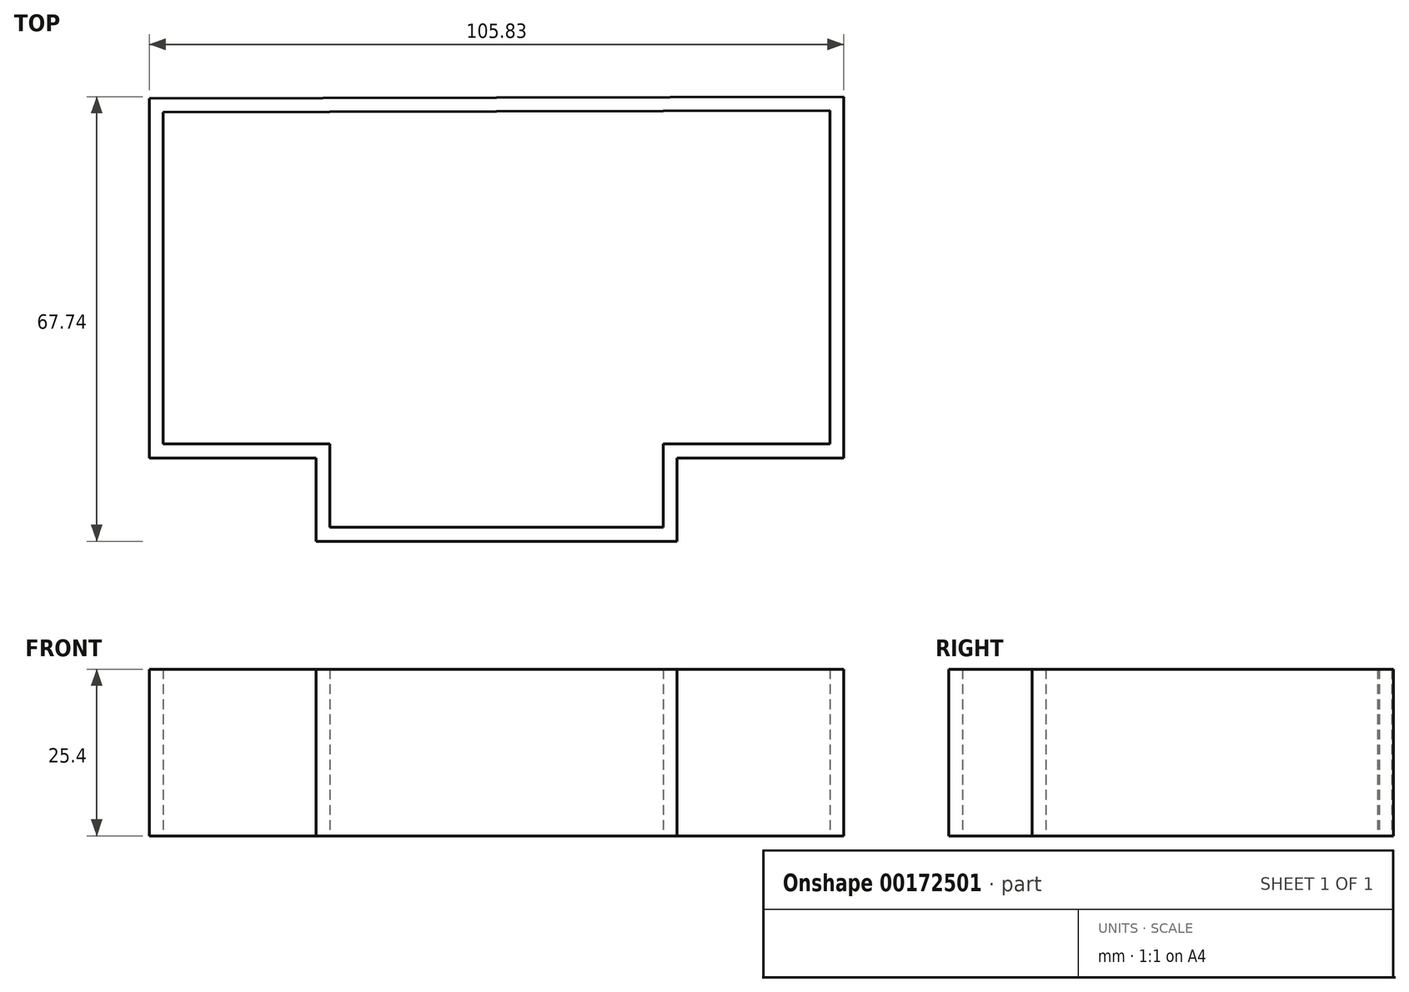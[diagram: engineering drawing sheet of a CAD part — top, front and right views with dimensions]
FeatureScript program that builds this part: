
annotation { "Feature Type Name" : "Feature", "Feature Type Description" : "" }
export const myFeature = defineFeature(function(context is Context, id is Id, definition is map)
    precondition{}
    {
        {
            var Q0;
            Q0=qCreatedBy(makeId("Top.planeOp"),FACE);
            var sketch = newSketch(context, id + "F0", { "sketchPlane" : qUnion([Q0])});
            skLineSegment(sketch, "E0", {"start": v(-70.38, 74.45) * mm, "end": v(-70.38, 23.9) * mm});
            skLineSegment(sketch, "E1", {"start": v(-70.38, 23.9) * mm, "end": v(-44.98, 23.9) * mm});
            skLineSegment(sketch, "E2", {"start": v(-44.98, 23.9) * mm, "end": v(-44.98, 11.2) * mm});
            skLineSegment(sketch, "E3", {"start": v(-44.98, 11.2) * mm, "end": v(5.82, 11.2) * mm});
            skLineSegment(sketch, "E4", {"start": v(5.82, 11.2) * mm, "end": v(5.82, 23.9) * mm});
            skLineSegment(sketch, "E5", {"start": v(5.82, 23.9) * mm, "end": v(31.22, 23.9) * mm});
            skLineSegment(sketch, "E6", {"start": v(31.22, 23.9) * mm, "end": v(31.22, 74.7) * mm});
            skLineSegment(sketch, "E7", {"start": v(31.22, 74.7) * mm, "end": v(-70.38, 74.45) * mm});
            skSolve(sketch);
        }
        {
            var Q0;
            Q0=qCreatedBy(makeId("Top.planeOp"),FACE);
            var sketch = newSketch(context, id + "F1", { "sketchPlane" : qUnion([Q0])});
            skLineSegment(sketch, "E8.0", {"start": v(33.34, 21.79) * mm, "end": v(33.34, 76.83) * mm});
            skLineSegment(sketch, "E8.1", {"start": v(7.94, 21.79) * mm, "end": v(33.34, 21.79) * mm});
            skLineSegment(sketch, "E8.2", {"start": v(33.34, 76.83) * mm, "end": v(-72.5, 76.56) * mm});
            skLineSegment(sketch, "E8.3", {"start": v(7.94, 9.09) * mm, "end": v(7.94, 21.79) * mm});
            skLineSegment(sketch, "E8.4", {"start": v(-72.5, 76.56) * mm, "end": v(-72.5, 21.79) * mm});
            skLineSegment(sketch, "E8.5", {"start": v(-72.5, 21.79) * mm, "end": v(-47.1, 21.79) * mm});
            skLineSegment(sketch, "E8.6", {"start": v(-47.1, 21.79) * mm, "end": v(-47.1, 9.09) * mm});
            skLineSegment(sketch, "E8.7", {"start": v(-47.1, 9.09) * mm, "end": v(7.94, 9.09) * mm});
            skSolve(sketch);
        }
        {
            var Q0;
            Q0=makeQuery(id+"F1.imprint","IMPRINT",FACE,{"disambiguationData":[TD([[makeQuery(id+"F1.imprint","IMPRINT",EDGE,{"derivedFrom":sQuery(id+"F1.wireOp",EDGE,"E8.0")}),1.0]])]});
            var Q1;
            Q1=makeQuery(id+"F0.imprint","IMPRINT",FACE,{"disambiguationData":[TD([[makeQuery(id+"F0.imprint","IMPRINT",EDGE,{"derivedFrom":sQuery(id+"F0.wireOp",EDGE,"E0")}),1.0]])]});
            extrude(context, id + "F2", {"entities" : qUnion([Q0, Q1]), "depth" : 25.4 * mm});
        }
    });
